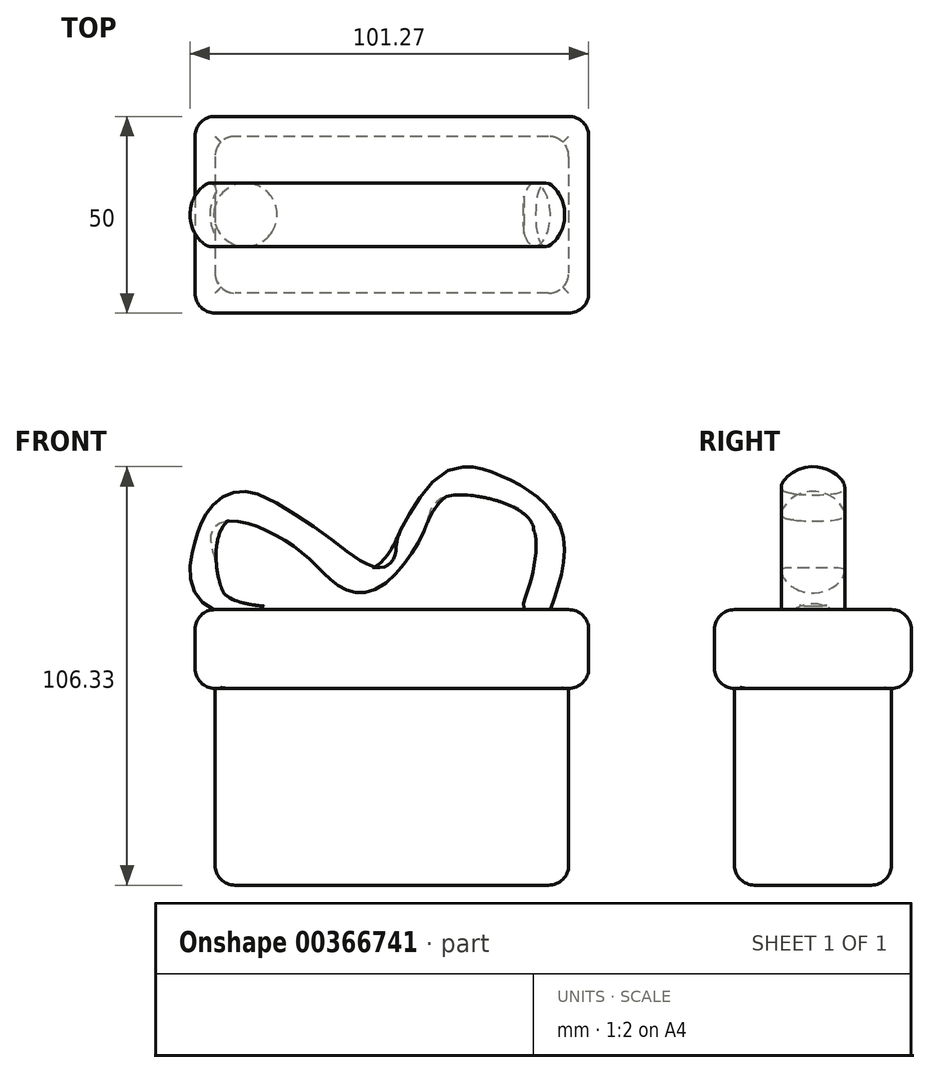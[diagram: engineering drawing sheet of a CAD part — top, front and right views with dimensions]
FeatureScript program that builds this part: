
annotation { "Feature Type Name" : "Feature", "Feature Type Description" : "" }
export const myFeature = defineFeature(function(context is Context, id is Id, definition is map)
    precondition{}
    {
        {
            var Q0;
            Q0=qCreatedBy(makeId("Top.planeOp"),FACE);
            var sketch = newSketch(context, id + "F0", { "sketchPlane" : qUnion([Q0])});
            skLineSegment(sketch, "E0.bottom", {"start": v(50, 25) * mm, "end": v(-50, 25) * mm});
            skLineSegment(sketch, "E0.top", {"start": v(50, -25) * mm, "end": v(-50, -25) * mm});
            skLineSegment(sketch, "E0.left", {"start": v(50, 25) * mm, "end": v(50, -25) * mm});
            skLineSegment(sketch, "E0.right", {"start": v(-50, 25) * mm, "end": v(-50, -25) * mm});
            skPoint(sketch, "E0.middle", {"position": v(0, 0) * mm});
            skSolve(sketch);
        }
        {
            var Q0;
            Q0=makeQuery(id+"F0.imprint","IMPRINT",FACE,{"disambiguationData":[TD([[makeQuery(id+"F0.imprint","IMPRINT",EDGE,{"derivedFrom":sQuery(id+"F0.wireOp",EDGE,"E0.bottom")}),1.0]])]});
            extrude(context, id + "F1", {"entities" : qUnion([Q0]), "oppositeDirection" : true, "depth" : 20 * mm});
        }
        {
            var Q0;
            Q0=makeQuery(id+"F1.opExtrude","SWEPT_FACE",FACE,{"disambiguationData":[OSD([sQuery(id+"F0.wireOp",EDGE,"E0.top")])]});
            var Q1;
            Q1=makeQuery(id+"F1.opExtrude","SWEPT_FACE",FACE,{"disambiguationData":[OSD([sQuery(id+"F0.wireOp",EDGE,"E0.left")])]});
            var Q2;
            Q2=makeQuery(id+"F1.opExtrude","SWEPT_FACE",FACE,{"disambiguationData":[OSD([sQuery(id+"F0.wireOp",EDGE,"E0.bottom")])]});
            var Q3;
            Q3=makeQuery(id+"F1.opExtrude","SWEPT_FACE",FACE,{"disambiguationData":[OSD([sQuery(id+"F0.wireOp",EDGE,"E0.right")])]});
            fillet(context, id + "F2", {"entities" : qUnion([Q0, Q1, Q2, Q3]), "radius" : 5.08 * mm, "tangentPropagation" : true, "allowEdgeOverflow" : false});
        }
        {
            var Q0;
            Q0=qCreatedBy(makeId("Top.planeOp"),FACE);
            var sketch = newSketch(context, id + "F3", { "sketchPlane" : qUnion([Q0])});
            skCircle(sketch, "E1", {"center": v(-37.2, 0) * mm, "radius": 8.05 * mm});
            skSolve(sketch);
        }
        {
            var Q0;
            Q0=qCreatedBy(makeId("Front.planeOp"),FACE);
            var sketch = newSketch(context, id + "F4", { "sketchPlane" : qUnion([Q0])});
            skFitSpline(sketch, "E2", {"points": [v(-37.2, 0) * mm, v(-45.43, 7.04) * mm, v(-41.41, 23.32) * mm, v(-20.3, 16.89) * mm, v(-5.03, 10.05) * mm, v(8.44, 24.53) * mm, v(18.9, 31.16) * mm, v(37.4, 21.51) * mm, v(34.18, -6.43) * mm], "startDerivative": vector(-105.98, 47.69) * mm, "endDerivative": vector(-69.45, -200.33) * mm});
            skSolve(sketch);
        }
        {
            var Q0;
            Q0=makeQuery(id+"F3.imprint","IMPRINT",FACE,{"disambiguationData":[TD([[makeQuery(id+"F3.imprint","IMPRINT",EDGE,{"derivedFrom":sQuery(id+"F3.wireOp",EDGE,"E1")}),1.0]])]});
            var Q1;
            Q1=sQuery(id+"F4.wireOp",EDGE,"E2");
            sweep(context, id + "F5", {"operationType" : NewBodyOperationType.ADD, "profiles" : qUnion([Q0]), "path" : qUnion([Q1])});
        }
        {
            var Q0;
            Q0=makeQuery(id+"F1.opExtrude","CAP_FACE",FACE,{"disambiguationData":[OSD([sQuery(id+"F0.wireOp",EDGE,"E0.bottom"),sQuery(id+"F0.wireOp",EDGE,"E0.top"),sQuery(id+"F0.wireOp",EDGE,"E0.left"),sQuery(id+"F0.wireOp",EDGE,"E0.right")])],"isStart":false});
            var sketch = newSketch(context, id + "F6", { "sketchPlane" : qUnion([Q0])});
            skLineSegment(sketch, "E3.bottom", {"start": v(44.92, 19.92) * mm, "end": v(-44.92, 19.92) * mm});
            skLineSegment(sketch, "E3.top", {"start": v(44.92, -19.92) * mm, "end": v(-44.92, -19.92) * mm});
            skLineSegment(sketch, "E3.left", {"start": v(44.92, 19.92) * mm, "end": v(44.92, -19.92) * mm});
            skLineSegment(sketch, "E3.right", {"start": v(-44.92, 19.92) * mm, "end": v(-44.92, -19.92) * mm});
            skPoint(sketch, "E3.middle", {"position": v(0, 0) * mm});
            skSolve(sketch);
        }
        {
            var Q0;
            Q0=makeQuery(id+"F6.imprint","IMPRINT",FACE,{"disambiguationData":[TD([[makeQuery(id+"F6.imprint","IMPRINT",EDGE,{"derivedFrom":sQuery(id+"F6.wireOp",EDGE,"E3.bottom")}),1.0]])]});
            var Q1;
            Q1=sQuery(id+"F6.wireOp",EDGE,"E3.bottom");
            var Q2;
            Q2=sQuery(id+"F6.wireOp",EDGE,"E3.left");
            extrude(context, id + "F7", {"entities" : qUnion([Q0]), "operationType" : NewBodyOperationType.ADD, "surfaceEntities" : qUnion([Q1, Q2]), "depth" : 50 * mm});
        }
        {
            var Q0;
            Q0=makeQuery(id+"F7.opExtrude","CAP_EDGE",EDGE,{"disambiguationData":[OSD([sQuery(id+"F6.wireOp",EDGE,"E3.left")])],"isStart":false});
            var Q1;
            Q1=makeQuery(id+"F7.opExtrude","SWEPT_EDGE",EDGE,{"disambiguationData":[OSD([sQuery(id+"F6.wireOp",EDGE,"E3.bottom"),sQuery(id+"F6.wireOp",EDGE,"E3.left")])]});
            var Q2;
            Q2=makeQuery(id+"F7.opExtrude","SWEPT_EDGE",EDGE,{"disambiguationData":[OSD([sQuery(id+"F6.wireOp",EDGE,"E3.top"),sQuery(id+"F6.wireOp",EDGE,"E3.left")])]});
            var Q3;
            Q3=makeQuery(id+"F7.opExtrude","SWEPT_EDGE",EDGE,{"disambiguationData":[OSD([sQuery(id+"F6.wireOp",EDGE,"E3.bottom"),sQuery(id+"F6.wireOp",EDGE,"E3.right")])]});
            var Q4;
            Q4=makeQuery(id+"F7.opExtrude","SWEPT_EDGE",EDGE,{"disambiguationData":[OSD([sQuery(id+"F6.wireOp",EDGE,"E3.top"),sQuery(id+"F6.wireOp",EDGE,"E3.right")])]});
            var Q5;
            Q5=makeQuery(id+"F7.opExtrude","CAP_EDGE",EDGE,{"disambiguationData":[OSD([sQuery(id+"F6.wireOp",EDGE,"E3.top")])],"isStart":false});
            var Q6;
            Q6=makeQuery(id+"F7.opExtrude","CAP_EDGE",EDGE,{"disambiguationData":[OSD([sQuery(id+"F6.wireOp",EDGE,"E3.right")])],"isStart":false});
            var Q7;
            Q7=makeQuery(id+"F7.opExtrude","CAP_EDGE",EDGE,{"disambiguationData":[OSD([sQuery(id+"F6.wireOp",EDGE,"E3.bottom")])],"isStart":false});
            fillet(context, id + "F8", {"entities" : qUnion([Q0, Q1, Q2, Q3, Q4, Q5, Q6, Q7]), "radius" : 5.08 * mm, "tangentPropagation" : true, "allowEdgeOverflow" : false});
        }
    });
